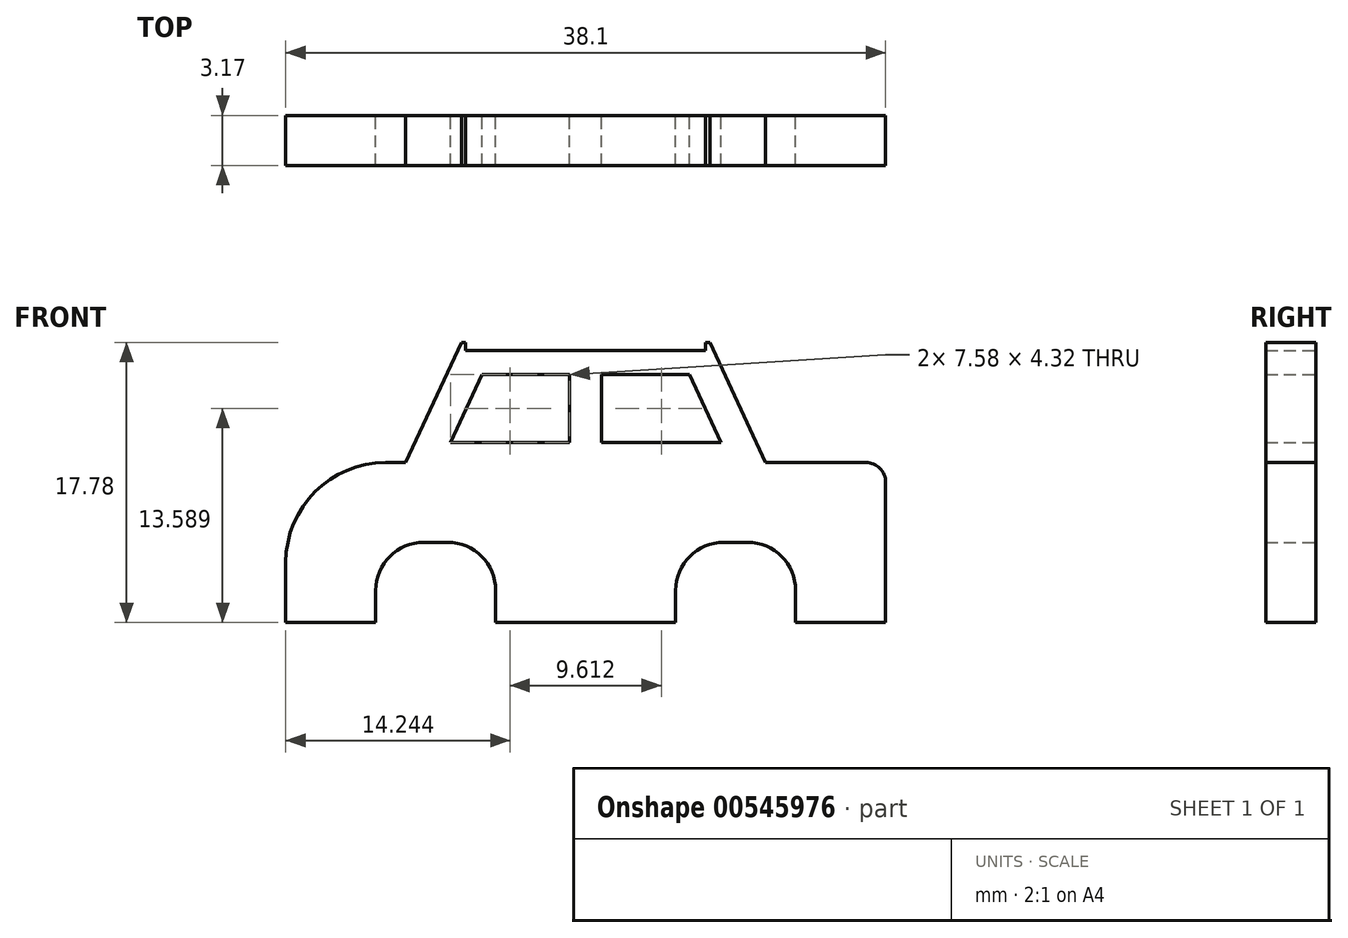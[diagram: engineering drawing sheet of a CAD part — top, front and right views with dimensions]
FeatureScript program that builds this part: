
annotation { "Feature Type Name" : "Feature", "Feature Type Description" : "" }
export const myFeature = defineFeature(function(context is Context, id is Id, definition is map)
    precondition{}
    {
        {
            var Q0;
            Q0=qCreatedBy(makeId("Front.planeOp"),FACE);
            var sketch = newSketch(context, id + "F0", { "sketchPlane" : qUnion([Q0])});
            skLineSegment(sketch, "E0.bottom", {"start": v(17.78, 5.08) * mm, "end": v(-12.7, 5.08) * mm});
            skLineSegment(sketch, "E0.top", {"start": v(19.05, -5.08) * mm, "end": v(-19.05, -5.08) * mm});
            skLineSegment(sketch, "E0.left", {"start": v(19.05, 3.81) * mm, "end": v(19.05, -5.08) * mm});
            skLineSegment(sketch, "E0.right", {"start": v(-19.05, -1.27) * mm, "end": v(-19.05, -5.08) * mm});
            skPoint(sketch, "E0.middle", {"position": v(0, 0) * mm});
            skLineSegment(sketch, "E1", {"start": v(-11.43, 5.08) * mm, "end": v(-11.43, -5.08) * mm, "construction": true});
            skLineSegment(sketch, "E2", {"start": v(-7.88, 12.7) * mm, "end": v(7.88, 12.7) * mm});
            skLineSegment(sketch, "E3", {"start": v(-11.43, 5.08) * mm, "end": v(-7.88, 12.7) * mm});
            skLineSegment(sketch, "E4", {"start": v(7.88, 12.7) * mm, "end": v(11.43, 5.08) * mm});
            skLineSegment(sketch, "E5", {"start": v(0, 12.7) * mm, "end": v(0, -5.08) * mm, "construction": true});
            skLineSegment(sketch, "E6", {"start": v(-8.6, 6.35) * mm, "end": v(-1.02, 6.35) * mm});
            skLineSegment(sketch, "E7", {"start": v(-1.02, 6.35) * mm, "end": v(-1.02, 10.67) * mm});
            skLineSegment(sketch, "E8", {"start": v(-1.02, 10.67) * mm, "end": v(-6.58, 10.67) * mm});
            skLineSegment(sketch, "E9", {"start": v(-6.58, 10.67) * mm, "end": v(-8.6, 6.35) * mm});
            skLineSegment(sketch, "E10.MirrorCS", {"start": v(0, 8.64) * mm, "end": v(0, 26.42) * mm, "construction": true});
            skLineSegment(sketch, "E11.MirrorCS", {"start": v(1.02, 6.35) * mm, "end": v(1.02, 10.67) * mm});
            skLineSegment(sketch, "E12.MirrorCS", {"start": v(8.6, 6.35) * mm, "end": v(1.02, 6.35) * mm});
            skLineSegment(sketch, "E13.MirrorCS", {"start": v(6.58, 10.67) * mm, "end": v(8.6, 6.35) * mm});
            skLineSegment(sketch, "E14.MirrorCS", {"start": v(1.02, 10.67) * mm, "end": v(6.58, 10.67) * mm});
            skPoint(sketch, "E15.visualSharp", {"position": v(-19.05, 5.08) * mm});
            skArc(sketch, "E15.filletArc", {"start": v(-12.7, 5.08) * mm, "mid": v(-17.2, 3.22) * mm, "end": v(-19.05, -1.27) * mm});
            skPoint(sketch, "E16.visualSharp", {"position": v(19.05, 5.08) * mm});
            skArc(sketch, "E16.filletArc", {"start": v(19.05, 3.81) * mm, "mid": v(18.68, 4.7) * mm, "end": v(17.78, 5.08) * mm});
            skLineSegment(sketch, "E17.bottom", {"start": v(-10.29, 0) * mm, "end": v(-8.76, 0) * mm});
            skLineSegment(sketch, "E17.top", {"start": v(-13.33, -5.08) * mm, "end": v(-5.71, -5.08) * mm});
            skLineSegment(sketch, "E17.left", {"start": v(-13.33, -3.05) * mm, "end": v(-13.33, -5.08) * mm});
            skLineSegment(sketch, "E17.right", {"start": v(-5.71, -3.05) * mm, "end": v(-5.71, -5.08) * mm});
            skPoint(sketch, "E18.visualSharp", {"position": v(-13.33, 0) * mm});
            skArc(sketch, "E18.filletArc", {"start": v(-10.29, 0) * mm, "mid": v(-12.44, -0.9) * mm, "end": v(-13.33, -3.05) * mm});
            skPoint(sketch, "E19.visualSharp", {"position": v(-5.71, 0) * mm});
            skArc(sketch, "E19.filletArc", {"start": v(-5.71, -3.05) * mm, "mid": v(-6.6, -0.9) * mm, "end": v(-8.76, 0) * mm});
            skArc(sketch, "E20.MirrorCS", {"start": v(5.72, -3.05) * mm, "mid": v(6.6, -0.9) * mm, "end": v(8.76, 0) * mm});
            skLineSegment(sketch, "E21.MirrorCS", {"start": v(10.29, 0) * mm, "end": v(8.76, 0) * mm});
            skArc(sketch, "E22.MirrorCS", {"start": v(10.29, 0) * mm, "mid": v(12.44, -0.9) * mm, "end": v(13.34, -3.05) * mm});
            skLineSegment(sketch, "E23.MirrorCS", {"start": v(13.34, -3.05) * mm, "end": v(13.34, -5.08) * mm});
            skLineSegment(sketch, "E24.MirrorCS", {"start": v(5.72, -3.05) * mm, "end": v(5.72, -5.08) * mm});
            skLineSegment(sketch, "E25.bottom", {"start": v(-7.62, 12.7) * mm, "end": v(0, 12.7) * mm});
            skLineSegment(sketch, "E25.top", {"start": v(-7.62, 12.2) * mm, "end": v(0, 12.2) * mm});
            skLineSegment(sketch, "E25.left", {"start": v(-7.62, 12.7) * mm, "end": v(-7.62, 12.2) * mm});
            skLineSegment(sketch, "E25.right", {"start": v(0, 12.7) * mm, "end": v(0, 12.2) * mm});
            skLineSegment(sketch, "E26.MirrorCS", {"start": v(7.62, 12.2) * mm, "end": v(0, 12.2) * mm});
            skLineSegment(sketch, "E27.MirrorCS", {"start": v(7.62, 12.7) * mm, "end": v(7.62, 12.2) * mm});
            skSolve(sketch);
        }
        {
            var Q0;
            {var subQ4=sQuery(id+"F0.wireOp",EDGE,"E0.left");Q0=makeQuery(id+"F0.imprint","IMPRINT",FACE,{"disambiguationData":[TD([[makeQuery(id+"F0.imprint","IMPRINT",EDGE,{"derivedFrom":subQ4}),-1.0]])]});}
            var Q1;
            Q1=makeQuery(id+"F0.imprint","IMPRINT",FACE,{"disambiguationData":[TD([[makeQuery(id+"F0.imprint","IMPRINT",EDGE,{"derivedFrom":sQuery(id+"F0.wireOp",EDGE,"E2")}),-1.0]])]});
            extrude(context, id + "F1", {"entities" : qUnion([Q0, Q1]), "depth" : 3.17 * mm, "offsetDistance" : 25.4 * mm});
        }
    });
